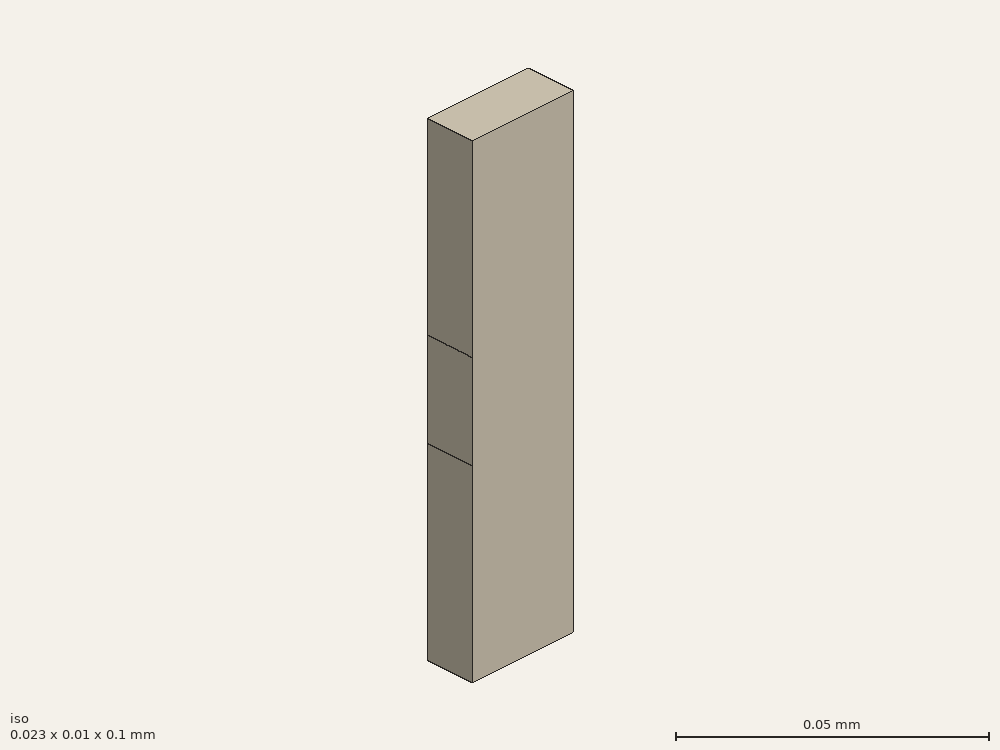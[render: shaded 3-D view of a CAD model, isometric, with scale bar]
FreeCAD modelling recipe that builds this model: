
FCSTD DOCUMENT  (FreeCAD 0.21R33694 (Git))
Label: straight
License: All rights reserved
LicenseURL: http://en.wikipedia.org/wiki/All_rights_reserved
objects: Part::Part2DObjectPython×6, App::FeaturePython×4, Part::Extrusion×2, Part::FeaturePython×2, Part::Cut×2
note: 12 computed .brp shape members not serialized (recipe doc carries the construction recipe); baked Part::Feature solids carry a one-line shape summary decoded from their .brp

FEATURE [Part::Part2DObjectPython] Rectangle  # Draft 2D object (typed FeaturePython)
  Area = 232.258
  ChamferSize = 0
  Columns = 1
  FilletRadius = 0
  Height = 10.16
  Length = 22.86
  MakeFace = true
  Placement = pos=(-11.43,-5.08,0) rot=(0,0,1;0rad)
  Rows = 1
FEATURE [Part::Extrusion] Extrude
  Base = -> Rectangle
  Dir = (0,0,1)
  DirMode = 2
  FaceMakerClass = Part::FaceMakerBullseye
  LengthFwd = 100
  LengthRev = 0
  Solid = false
  Symmetric = false
FEATURE [Part::Part2DObjectPython] Rectangle001  label="_Pport1"  # Draft 2D object (typed FeaturePython)
  Area = 0.000232258
  ChamferSize = 0
  Columns = 1
  FilletRadius = 0
  Height = 0.01016
  Length = 0.02286
  MakeFace = true
  Placement = pos=(-0.01143,-0.00508,0.1) rot=(0,0,1;0rad)
  Rows = 1
FEATURE [Part::Part2DObjectPython] Line  label="_Pv1"  # Draft 2D object (typed FeaturePython)
  Area = 0
  ChamferSize = 0
  Closed = false
  End = (-1.8e-15,0.00508,0.1)
  FilletRadius = 0
  Length = 0.01016
  MakeFace = true
  Placement = pos=(0,-0.00508,0.1) rot=(0,0,1;0rad)
  Points = (2) [(0,0,0),(-1.77605e-15,0.01016,0)]
  Start = (0,-0.00508,0.1)
  Subdivisions = 0
FEATURE [Part::Part2DObjectPython] Rectangle002  label="_Pport2"  # Draft 2D object (typed FeaturePython)
  Area = 0.000232258
  ChamferSize = 0
  Columns = 1
  FilletRadius = 0
  Height = 0.01016
  Length = 0.02286
  MakeFace = true
  Placement = pos=(-0.01143,-0.00508,0) rot=(0,0,1;0rad)
  Rows = 1
FEATURE [Part::Part2DObjectPython] Line001  label="_Pv2"  # Draft 2D object (typed FeaturePython)
  Area = 0
  ChamferSize = 0
  Closed = false
  End = (0,0.00508,0)
  FilletRadius = 0
  Length = 0.01016
  MakeFace = true
  Placement = pos=(0,-0.00508,0) rot=(0,0,1;0rad)
  Points = (2) [(0,0,0),(3.1106e-19,0.01016,0)]
  Start = (0,-0.00508,0)
  Subdivisions = 0
FEATURE [App::FeaturePython] Text  label="_Sinput(PV){port1}"  # WARN: FeaturePython — macro-defined, semantics opaque (R4)
  Placement = pos=(0.0413747,-0.017509,0) rot=(0,0,1;0rad)
  Text = .
FEATURE [App::FeaturePython] Text001  label="_Soutput(PV){port2}"  # WARN: FeaturePython — macro-defined, semantics opaque (R4)
  Placement = pos=(0.0413747,-0.017509,0) rot=(0,0,1;0rad)
  Text = .
FEATURE [App::FeaturePython] Text002  label="_Linput(1,voltage){v1}"  # WARN: FeaturePython — macro-defined, semantics opaque (R4)
  Placement = pos=(0.0413747,-0.017509,0) rot=(0,0,1;0rad)
  Text = .
FEATURE [App::FeaturePython] Text003  label="_Loutput(2,voltage){v2}"  # WARN: FeaturePython — macro-defined, semantics opaque (R4)
  Placement = pos=(0.0413747,-0.017509,0) rot=(0,0,1;0rad)
  Text = .
FEATURE [Part::Part2DObjectPython] Rectangle003  # Draft 2D object (typed FeaturePython)
  Area = 203.2
  ChamferSize = 0
  Columns = 1
  FilletRadius = 0
  Height = 20
  Length = 10.16
  MakeFace = true
  Placement = pos=(11.43,-5.08,40) rot=(0.57735,0.57735,0.57735;2.0944rad)
  Rows = 1
FEATURE [Part::Extrusion] Extrude001
  Base = -> Rectangle003
  Dir = (1,0,0)
  DirMode = 2
  FaceMakerClass = Part::FaceMakerBullseye
  LengthFwd = 0.01
  LengthRev = 0
  Placement = pos=(-0.01,0,0) rot=(0,0,1;0rad)
  Solid = false
  Symmetric = false
FEATURE [Part::FeaturePython] Clone  label="Extrude002"  # Draft clone (typed FeaturePython)
  AttacherType = Attacher::AttachEngine3D
  Fuse = false
  Objects = -> [Extrude001]
  Placement = pos=(-22.86,-1.8e-15,0) rot=(0,0,1;0rad)
  Scale = (1,1,1)
FEATURE [Part::Cut] Cut
  Base = -> Extrude
  Tool = -> Extrude001
FEATURE [Part::Cut] Cut001
  Base = -> Cut
  Tool = -> Clone
FEATURE [Part::FeaturePython] Clone001  label="scaled"  # Draft clone (typed FeaturePython)
  AttacherType = Attacher::AttachEngine3D
  Fuse = false
  Objects = -> [Cut001]
  Scale = (0.001,0.001,0.001)
